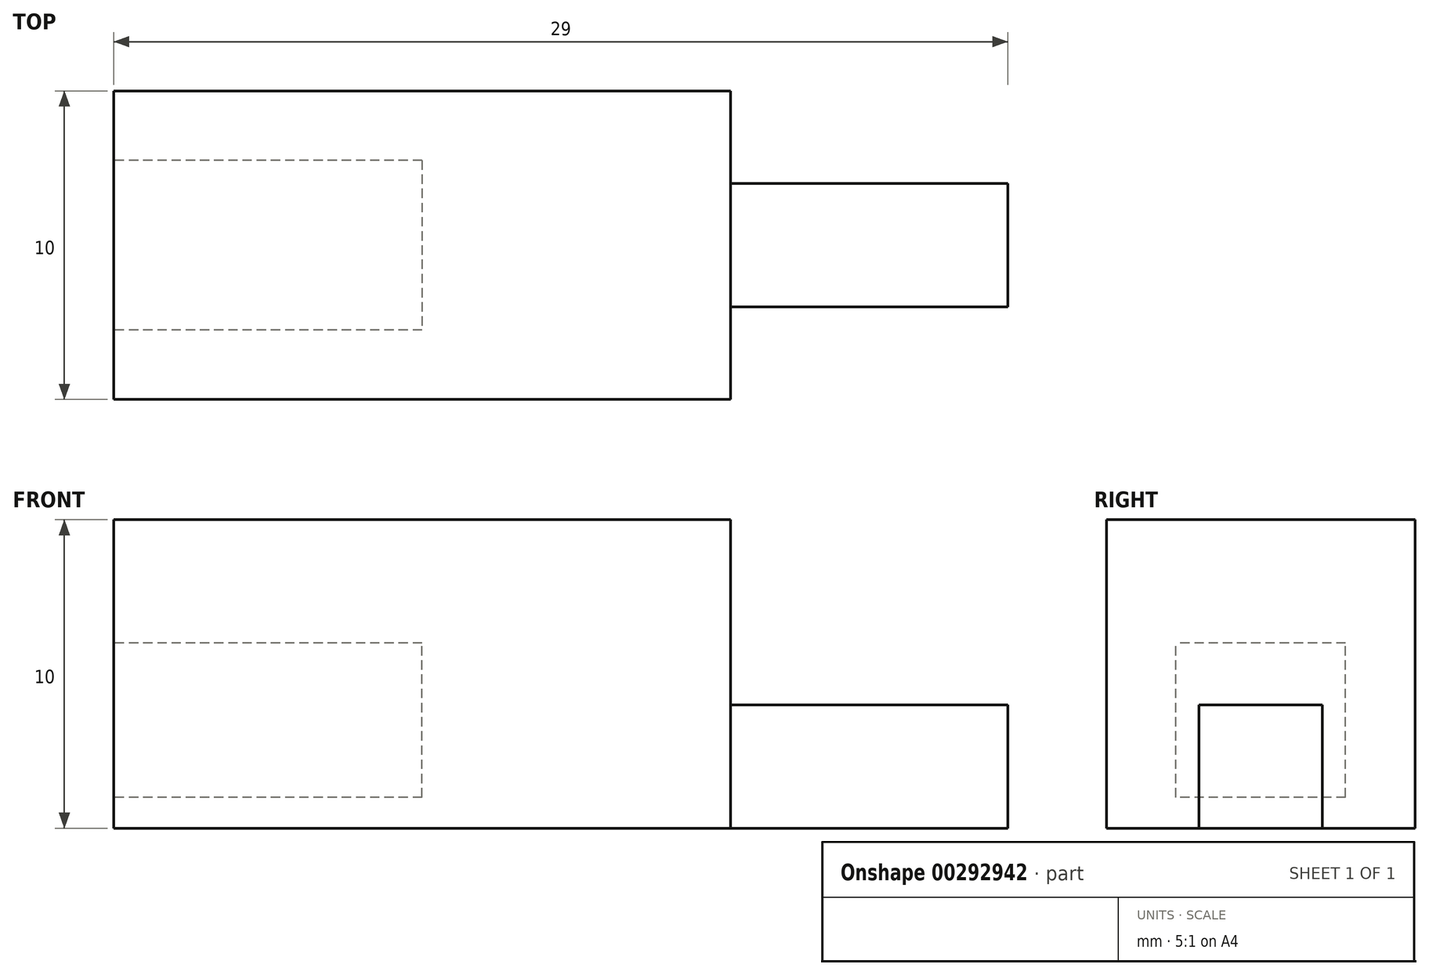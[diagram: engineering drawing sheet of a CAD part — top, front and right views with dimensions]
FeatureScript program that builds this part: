
annotation { "Feature Type Name" : "Feature", "Feature Type Description" : "" }
export const myFeature = defineFeature(function(context is Context, id is Id, definition is map)
    precondition{}
    {
        {
            var Q0;
            Q0=qCreatedBy(makeId("Top.planeOp"),FACE);
            var sketch = newSketch(context, id + "F0", { "sketchPlane" : qUnion([Q0])});
            skLineSegment(sketch, "E0.bottom", {"start": v(0, 0) * mm, "end": v(20, 0) * mm});
            skLineSegment(sketch, "E0.top", {"start": v(0, 10) * mm, "end": v(20, 10) * mm});
            skLineSegment(sketch, "E0.left", {"start": v(0, 0) * mm, "end": v(0, 10) * mm});
            skLineSegment(sketch, "E0.right", {"start": v(20, 0) * mm, "end": v(20, 10) * mm});
            skSolve(sketch);
        }
        {
            var Q0;
            Q0 = qSketchRegion(id + "F0", true);
            extrude(context, id + "F1", {"entities" : qUnion([Q0]), "depth" : 10 * mm, "offsetDistance" : 25 * mm});
        }
        {
            var Q0;
            Q0=makeQuery(id+"F1.opExtrude","SWEPT_FACE",FACE,{"disambiguationData":[OSD([sQuery(id+"F0.wireOp",EDGE,"E0.right")])]});
            var sketch = newSketch(context, id + "F2", { "sketchPlane" : qUnion([Q0])});
            skLineSegment(sketch, "E1.bottom", {"start": v(3, 0) * mm, "end": v(7, 0) * mm});
            skLineSegment(sketch, "E1.top", {"start": v(3, 4) * mm, "end": v(7, 4) * mm});
            skLineSegment(sketch, "E1.left", {"start": v(3, 0) * mm, "end": v(3, 4) * mm});
            skLineSegment(sketch, "E1.right", {"start": v(7, 0) * mm, "end": v(7, 4) * mm});
            skSolve(sketch);
        }
        {
            var Q0;
            Q0 = qSketchRegion(id + "F2", true);
            extrude(context, id + "F3", {"entities" : qUnion([Q0]), "operationType" : NewBodyOperationType.ADD, "depth" : 9 * mm, "offsetDistance" : 25 * mm});
        }
        {
            var Q0;
            Q0=makeQuery(id+"F1.opExtrude","SWEPT_FACE",FACE,{"disambiguationData":[OSD([sQuery(id+"F0.wireOp",EDGE,"E0.left")])]});
            var sketch = newSketch(context, id + "F4", { "sketchPlane" : qUnion([Q0])});
            skLineSegment(sketch, "E2.bottom", {"start": v(-7.75, 1) * mm, "end": v(-2.25, 1) * mm});
            skLineSegment(sketch, "E2.top", {"start": v(-7.75, 6) * mm, "end": v(-2.25, 6) * mm});
            skLineSegment(sketch, "E2.left", {"start": v(-7.75, 1) * mm, "end": v(-7.75, 6) * mm});
            skLineSegment(sketch, "E2.right", {"start": v(-2.25, 1) * mm, "end": v(-2.25, 6) * mm});
            skSolve(sketch);
        }
        {
            var Q0;
            Q0 = qSketchRegion(id + "F4", true);
            extrude(context, id + "F5", {"entities" : qUnion([Q0]), "operationType" : NewBodyOperationType.REMOVE, "oppositeDirection" : true, "depth" : 10 * mm, "offsetDistance" : 25 * mm});
        }
    });
